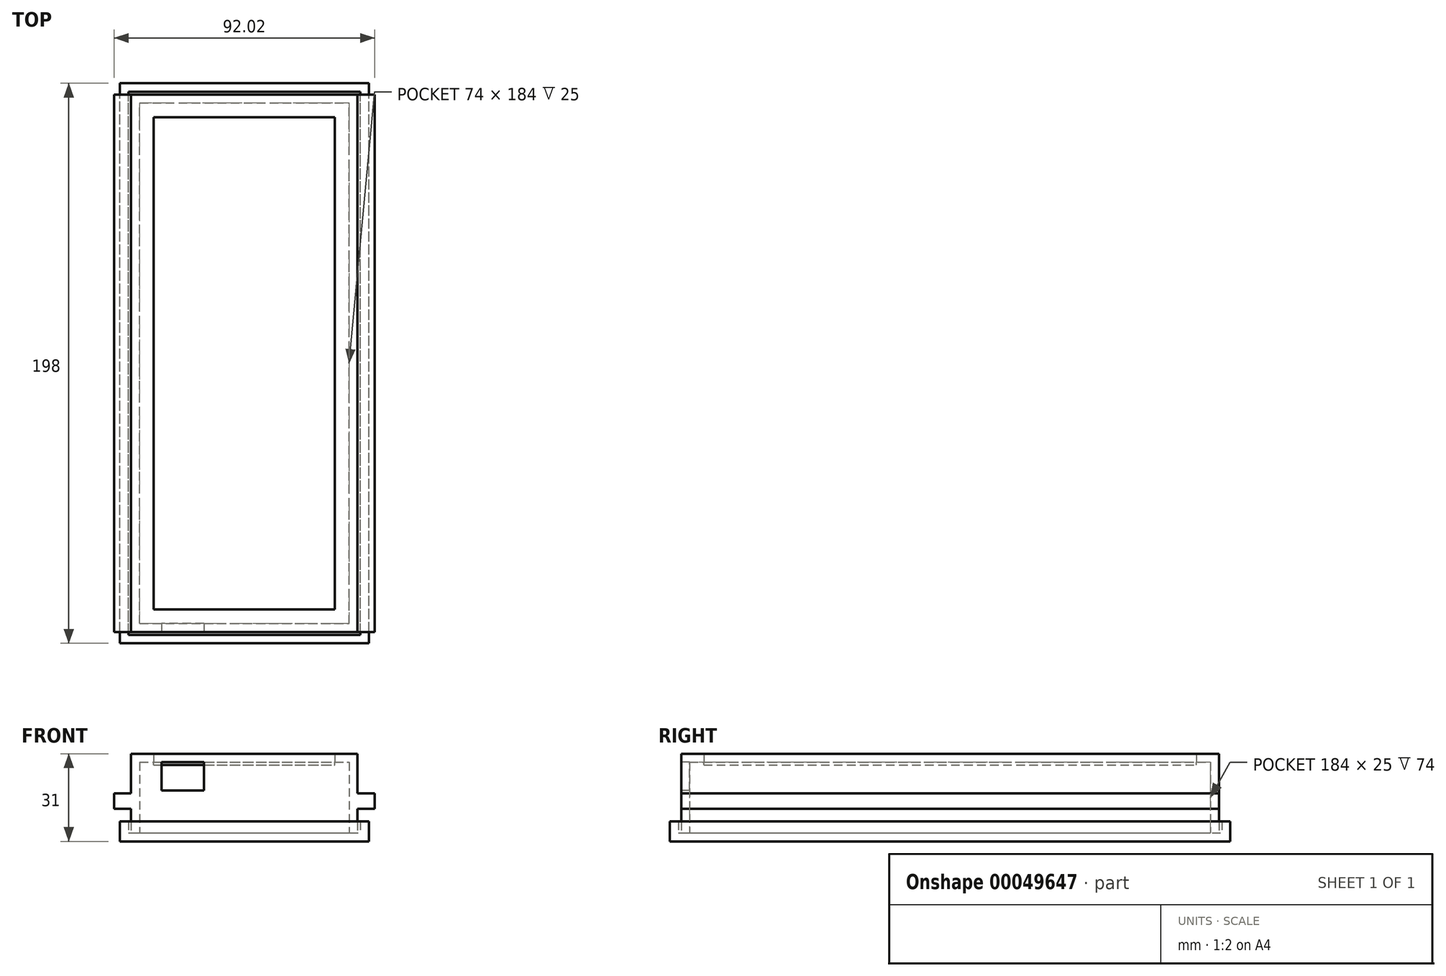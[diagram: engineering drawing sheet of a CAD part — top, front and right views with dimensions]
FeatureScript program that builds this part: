
annotation { "Feature Type Name" : "Feature", "Feature Type Description" : "" }
export const myFeature = defineFeature(function(context is Context, id is Id, definition is map)
    precondition{}
    {
        {
            var Q0;
            Q0=qCreatedBy(makeId("Top.planeOp"),FACE);
            var sketch = newSketch(context, id + "F0", { "sketchPlane" : qUnion([Q0])});
            skLineSegment(sketch, "E0.bottom", {"start": v(0, 0) * mm, "end": v(80, 0) * mm});
            skLineSegment(sketch, "E0.top", {"start": v(0, 190) * mm, "end": v(80, 190) * mm});
            skLineSegment(sketch, "E0.left", {"start": v(0, 0) * mm, "end": v(0, 190) * mm});
            skLineSegment(sketch, "E0.right", {"start": v(80, 0) * mm, "end": v(80, 190) * mm});
            skLineSegment(sketch, "E1.0", {"start": v(3, 3) * mm, "end": v(3, 187) * mm});
            skLineSegment(sketch, "E1.1", {"start": v(3, 3) * mm, "end": v(77, 3) * mm});
            skLineSegment(sketch, "E1.2", {"start": v(77, 3) * mm, "end": v(77, 187) * mm});
            skLineSegment(sketch, "E1.3", {"start": v(3, 187) * mm, "end": v(77, 187) * mm});
            skSolve(sketch);
        }
        {
            var Q0;
            Q0=makeQuery(id+"F0.imprint","IMPRINT",FACE,{"disambiguationData":[TD([[makeQuery(id+"F0.imprint","IMPRINT",EDGE,{"derivedFrom":sQuery(id+"F0.wireOp",EDGE,"15ba1adb-6d6a-4fff-ba81-59016011d17a.0")}),1.0]])]});
            var Q1;
            Q1=makeQuery(id+"F0.imprint","IMPRINT",FACE,{"disambiguationData":[TD([[makeQuery(id+"F0.imprint","IMPRINT",EDGE,{"derivedFrom":sQuery(id+"F0.wireOp",EDGE,"E0.bottom")}),1.0]])]});
            extrude(context, id + "F1", {"entities" : qUnion([Q0, Q1]), "depth" : 25 * mm});
        }
        {
            var Q0;
            Q0=makeQuery(id+"F1.opExtrude","CAP_FACE",FACE,{"disambiguationData":[OSD([sQuery(id+"F0.wireOp",EDGE,"E0.bottom"),sQuery(id+"F0.wireOp",EDGE,"E0.top"),sQuery(id+"F0.wireOp",EDGE,"E0.left"),sQuery(id+"F0.wireOp",EDGE,"E0.right")])],"isStart":false});
            var sketch = newSketch(context, id + "F2", { "sketchPlane" : qUnion([Q0])});
            skLineSegment(sketch, "E2.0", {"start": v(0, 190) * mm, "end": v(80, 190) * mm});
            skLineSegment(sketch, "E3.0", {"start": v(80, 0) * mm, "end": v(80, 190) * mm});
            skLineSegment(sketch, "E4.0", {"start": v(0, 0) * mm, "end": v(80, 0) * mm});
            skLineSegment(sketch, "E5.0", {"start": v(0, 0) * mm, "end": v(0, 190) * mm});
            skLineSegment(sketch, "E6.0", {"start": v(8, 182) * mm, "end": v(72, 182) * mm});
            skLineSegment(sketch, "E6.1", {"start": v(8, 8) * mm, "end": v(8, 182) * mm});
            skLineSegment(sketch, "E6.2", {"start": v(8, 8) * mm, "end": v(72, 8) * mm});
            skLineSegment(sketch, "E6.3", {"start": v(72, 8) * mm, "end": v(72, 182) * mm});
            skSolve(sketch);
        }
        {
            var Q0;
            Q0 = qSketchRegion(id + "F2", true);
            extrude(context, id + "F3", {"entities" : qUnion([Q0]), "operationType" : NewBodyOperationType.ADD, "depth" : 3 * mm});
        }
        {
            var Q0;
            Q0=qCreatedBy(makeId("Top.planeOp"),FACE);
            var sketch = newSketch(context, id + "F4", { "sketchPlane" : qUnion([Q0])});
            skLineSegment(sketch, "E7", {"start": v(0, 0) * mm, "end": v(-15.65, 9.04) * mm});
            skSolve(sketch);
        }
        {
            var Q0;
            Q0=sQuery(id+"F4.wireOp",VERTEX,"E7.end");
            var Q1;
            Q1=sQuery(id+"F4.wireOp",VERTEX,"E7.start");
            var Q2;
            Q2=makeQuery(id+"F3.opExtrude","CAP_VERTEX",VERTEX,{"disambiguationData":[OSD([sQuery(id+"F2.wireOp",EDGE,"E4.0"),sQuery(id+"F2.wireOp",EDGE,"E5.0")])],"isStart":false});
            cPlane(context, id + "F5", {"entities" : qUnion([Q0, Q1, Q2]), "cplaneType" : CPlaneType.THREE_POINT, "offset" : 150 * mm, "width" : 150 * mm, "height" : 150 * mm});
        }
        {
            var Q0;
            Q0=makeQuery(id+"F1.opExtrude","CAP_FACE",FACE,{"disambiguationData":[OSD([sQuery(id+"F0.wireOp",EDGE,"E0.bottom"),sQuery(id+"F0.wireOp",EDGE,"E0.top"),sQuery(id+"F0.wireOp",EDGE,"E0.left"),sQuery(id+"F0.wireOp",EDGE,"E0.right"),sQuery(id+"F0.wireOp",EDGE,"E1.0"),sQuery(id+"F0.wireOp",EDGE,"E1.1"),sQuery(id+"F0.wireOp",EDGE,"E1.2"),sQuery(id+"F0.wireOp",EDGE,"E1.3")])],"isStart":true});
            var sketch = newSketch(context, id + "F6", { "sketchPlane" : qUnion([Q0])});
            skLineSegment(sketch, "E8.0", {"start": v(-4, -194) * mm, "end": v(84, -194) * mm});
            skLineSegment(sketch, "E8.1", {"start": v(-4, 4) * mm, "end": v(-4, -194) * mm});
            skLineSegment(sketch, "E8.2", {"start": v(-4, 4) * mm, "end": v(84, 4) * mm});
            skLineSegment(sketch, "E8.3", {"start": v(84, 4) * mm, "end": v(84, -194) * mm});
            skLineSegment(sketch, "E9.0", {"start": v(-1, -191) * mm, "end": v(81, -191) * mm});
            skLineSegment(sketch, "E9.1", {"start": v(-1, 1) * mm, "end": v(-1, -191) * mm});
            skLineSegment(sketch, "E9.2", {"start": v(-1, 1) * mm, "end": v(81, 1) * mm});
            skLineSegment(sketch, "E9.3", {"start": v(81, 1) * mm, "end": v(81, -191) * mm});
            skSolve(sketch);
        }
        {
            var Q0;
            Q0=makeQuery(id+"F6.imprint","IMPRINT",FACE,{"disambiguationData":[TD([[makeQuery(id+"F6.imprint","IMPRINT",EDGE,{"derivedFrom":sQuery(id+"F6.wireOp",EDGE,"E8.0")}),1.0]])]});
            extrude(context, id + "F7", {"entities" : qUnion([Q0]), "oppositeDirection" : true, "depth" : 4 * mm});
        }
        {
            var Q0;
            Q0=makeQuery(id+"F6.imprint","IMPRINT",FACE,{"disambiguationData":[TD([[makeQuery(id+"F6.imprint","IMPRINT",EDGE,{"derivedFrom":sQuery(id+"F6.wireOp",EDGE,"E8.0")}),1.0]])]});
            var Q1;
            Q1=makeQuery(id+"F6.imprint","IMPRINT",FACE,{"disambiguationData":[TD([[makeQuery(id+"F6.imprint","IMPRINT",EDGE,{"derivedFrom":makeQuery(id+"F1.opExtrude","CAP_EDGE",EDGE,{"disambiguationData":[OSD([sQuery(id+"F0.wireOp",EDGE,"E1.0")])],"isStart":true})}),1.0]])]});
            var Q2;
            Q2=makeQuery(id+"F6.imprint","IMPRINT",FACE,{"disambiguationData":[TD([[makeQuery(id+"F6.imprint","IMPRINT",EDGE,{"derivedFrom":sQuery(id+"F6.wireOp",EDGE,"E9.0")}),1.0]])]});
            var Q3;
            Q3=makeQuery(id+"F6.imprint","IMPRINT",FACE,{"disambiguationData":[TD([[makeQuery(id+"F6.imprint","IMPRINT",EDGE,{"derivedFrom":makeQuery(id+"F1.opExtrude","CAP_EDGE",EDGE,{"disambiguationData":[OSD([sQuery(id+"F0.wireOp",EDGE,"E0.bottom")])],"isStart":true})}),-1.0]])]});
            extrude(context, id + "F8", {"entities" : qUnion([Q0, Q1, Q2, Q3]), "operationType" : NewBodyOperationType.ADD, "depth" : 3 * mm});
        }
        {
            var Q0;
            Q0=makeQuery(id+"F3.boolean.opBoolean","MERGE",FACE,{"derivedFrom":[makeQuery(id+"F1.opExtrude","SWEPT_FACE",FACE,{"disambiguationData":[OSD([sQuery(id+"F0.wireOp",EDGE,"E0.top")])]}),makeQuery(id+"F3.opExtrude","SWEPT_FACE",FACE,{"disambiguationData":[OSD([sQuery(id+"F2.wireOp",EDGE,"E2.0")])]})]});
            var sketch = newSketch(context, id + "F9", { "sketchPlane" : qUnion([Q0])});
            skLineSegment(sketch, "E10.bottom", {"start": v(0, 8.5) * mm, "end": v(6.01, 8.5) * mm});
            skLineSegment(sketch, "E10.top", {"start": v(0, 13.92) * mm, "end": v(6.01, 13.92) * mm});
            skLineSegment(sketch, "E10.left", {"start": v(0, 8.5) * mm, "end": v(0, 13.92) * mm});
            skLineSegment(sketch, "E10.right", {"start": v(6.01, 8.5) * mm, "end": v(6.01, 13.92) * mm});
            skLineSegment(sketch, "E11", {"start": v(-40, 28) * mm, "end": v(-40, 0) * mm, "construction": true});
            skLineSegment(sketch, "E12.MirrorCS", {"start": v(-80, 8.5) * mm, "end": v(-86.01, 8.5) * mm});
            skLineSegment(sketch, "E13.MirrorCS", {"start": v(-86.01, 8.5) * mm, "end": v(-86.01, 13.92) * mm});
            skLineSegment(sketch, "E14.MirrorCS", {"start": v(-80, 13.92) * mm, "end": v(-86.01, 13.92) * mm});
            skLineSegment(sketch, "E15.MirrorCS", {"start": v(-80, 8.5) * mm, "end": v(-80, 13.92) * mm});
            skSolve(sketch);
        }
        {
            var Q0;
            Q0=makeQuery(id+"F9.imprint","IMPRINT",FACE,{"disambiguationData":[TD([[makeQuery(id+"F9.imprint","IMPRINT",EDGE,{"derivedFrom":sQuery(id+"F9.wireOp",EDGE,"E10.bottom")}),1.0]])]});
            var Q1;
            Q1=makeQuery(id+"F9.imprint","IMPRINT",FACE,{"disambiguationData":[TD([[makeQuery(id+"F9.imprint","IMPRINT",EDGE,{"derivedFrom":sQuery(id+"F9.wireOp",EDGE,"E12.MirrorCS")}),-1.0]])]});
            var Q2;
            Q2=makeQuery(id+"F3.boolean.opBoolean","MERGE",FACE,{"derivedFrom":[makeQuery(id+"F1.opExtrude","SWEPT_FACE",FACE,{"disambiguationData":[OSD([sQuery(id+"F0.wireOp",EDGE,"E0.bottom")])]}),makeQuery(id+"F3.opExtrude","SWEPT_FACE",FACE,{"disambiguationData":[OSD([sQuery(id+"F2.wireOp",EDGE,"E4.0")])]})]});
            extrude(context, id + "F10", {"entities" : qUnion([Q0, Q1]), "operationType" : NewBodyOperationType.ADD, "endBound" : BoundingType.UP_TO_SURFACE, "oppositeDirection" : true, "endBoundEntityFace" : qUnion([Q2]), "depth" : 25 * mm});
        }
        {
            var Q0;
            {var subQ0=sQuery(id+"F2.wireOp",EDGE,"E4.0");var subQ1=sQuery(id+"F0.wireOp",EDGE,"E0.bottom");Q0=makeQuery(id+"F10.boolean.opBoolean","MERGE",FACE,{"derivedFrom":[makeQuery(id+"F3.boolean.opBoolean","MERGE",FACE,{"derivedFrom":[makeQuery(id+"F1.opExtrude","SWEPT_FACE",FACE,{"disambiguationData":[OSD([subQ1])]}),makeQuery(id+"F3.opExtrude","SWEPT_FACE",FACE,{"disambiguationData":[OSD([subQ0])]})]}),makeQuery(id+"F10.opExtrude","CAP_FACE",FACE,{"disambiguationData":[OSD([subQ1,subQ0]),ownerDisambiguation([makeQuery(id+"F10.opExtrude","SWEPT_BODY",BODY,{"disambiguationData":[OSD([sQuery(id+"F9.wireOp",EDGE,"E10.bottom"),sQuery(id+"F9.wireOp",EDGE,"E10.top"),sQuery(id+"F9.wireOp",EDGE,"E10.left"),sQuery(id+"F9.wireOp",EDGE,"E10.right")])]})])],"isStart":false}),makeQuery(id+"F10.opExtrude","CAP_FACE",FACE,{"disambiguationData":[OSD([subQ1,subQ0]),ownerDisambiguation([makeQuery(id+"F10.opExtrude","SWEPT_BODY",BODY,{"disambiguationData":[OSD([sQuery(id+"F9.wireOp",EDGE,"E12.MirrorCS"),sQuery(id+"F9.wireOp",EDGE,"E13.MirrorCS"),sQuery(id+"F9.wireOp",EDGE,"E14.MirrorCS"),sQuery(id+"F9.wireOp",EDGE,"E15.MirrorCS")])]})])],"isStart":false})]});}
            var sketch = newSketch(context, id + "F11", { "sketchPlane" : qUnion([Q0])});
            skLineSegment(sketch, "E16.bottom", {"start": v(25.7, 15) * mm, "end": v(10.7, 15) * mm});
            skLineSegment(sketch, "E16.top", {"start": v(25.7, 25) * mm, "end": v(10.7, 25) * mm});
            skLineSegment(sketch, "E16.left", {"start": v(25.7, 15) * mm, "end": v(25.7, 25) * mm});
            skLineSegment(sketch, "E16.right", {"start": v(10.7, 15) * mm, "end": v(10.7, 25) * mm});
            skSolve(sketch);
        }
        {
            var Q0;
            Q0=makeQuery(id+"F11.imprint","IMPRINT",FACE,{"disambiguationData":[TD([[makeQuery(id+"F11.imprint","IMPRINT",EDGE,{"derivedFrom":sQuery(id+"F11.wireOp",EDGE,"E16.bottom")}),-1.0]])]});
            extrude(context, id + "F12", {"entities" : qUnion([Q0]), "operationType" : NewBodyOperationType.REMOVE, "endBound" : BoundingType.UP_TO_NEXT, "oppositeDirection" : true, "depth" : 25 * mm});
        }
        {
            var Q0;
            Q0=makeQuery(id+"F3.opExtrude","CAP_FACE",FACE,{"disambiguationData":[OSD([sQuery(id+"F2.wireOp",EDGE,"E2.0"),sQuery(id+"F2.wireOp",EDGE,"E3.0"),sQuery(id+"F2.wireOp",EDGE,"E4.0"),sQuery(id+"F2.wireOp",EDGE,"E5.0"),sQuery(id+"F2.wireOp",EDGE,"E6.0"),sQuery(id+"F2.wireOp",EDGE,"E6.1"),sQuery(id+"F2.wireOp",EDGE,"E6.2"),sQuery(id+"F2.wireOp",EDGE,"E6.3")])],"isStart":true});
            var sketch = newSketch(context, id + "F13", { "sketchPlane" : qUnion([Q0])});
            skLineSegment(sketch, "E17.bottom", {"start": v(5.38, -5.46) * mm, "end": v(74.65, -5.46) * mm});
            skLineSegment(sketch, "E17.top", {"start": v(5.38, -184.04) * mm, "end": v(74.65, -184.04) * mm});
            skLineSegment(sketch, "E17.left", {"start": v(5.38, -5.46) * mm, "end": v(5.38, -184.04) * mm});
            skLineSegment(sketch, "E17.right", {"start": v(74.65, -5.46) * mm, "end": v(74.65, -184.04) * mm});
            skSolve(sketch);
        }
        {
            var Q0;
            Q0=makeQuery(id+"F13.imprint","IMPRINT",FACE,{"disambiguationData":[TD([[makeQuery(id+"F13.imprint","IMPRINT",EDGE,{"derivedFrom":makeQuery(id+"F3.opExtrude","CAP_EDGE",EDGE,{"disambiguationData":[OSD([sQuery(id+"F2.wireOp",EDGE,"E6.0")])],"isStart":true})}),1.0]])]});
            extrude(context, id + "F14", {"entities" : qUnion([Q0]), "depth" : 1 * mm});
        }
    });
